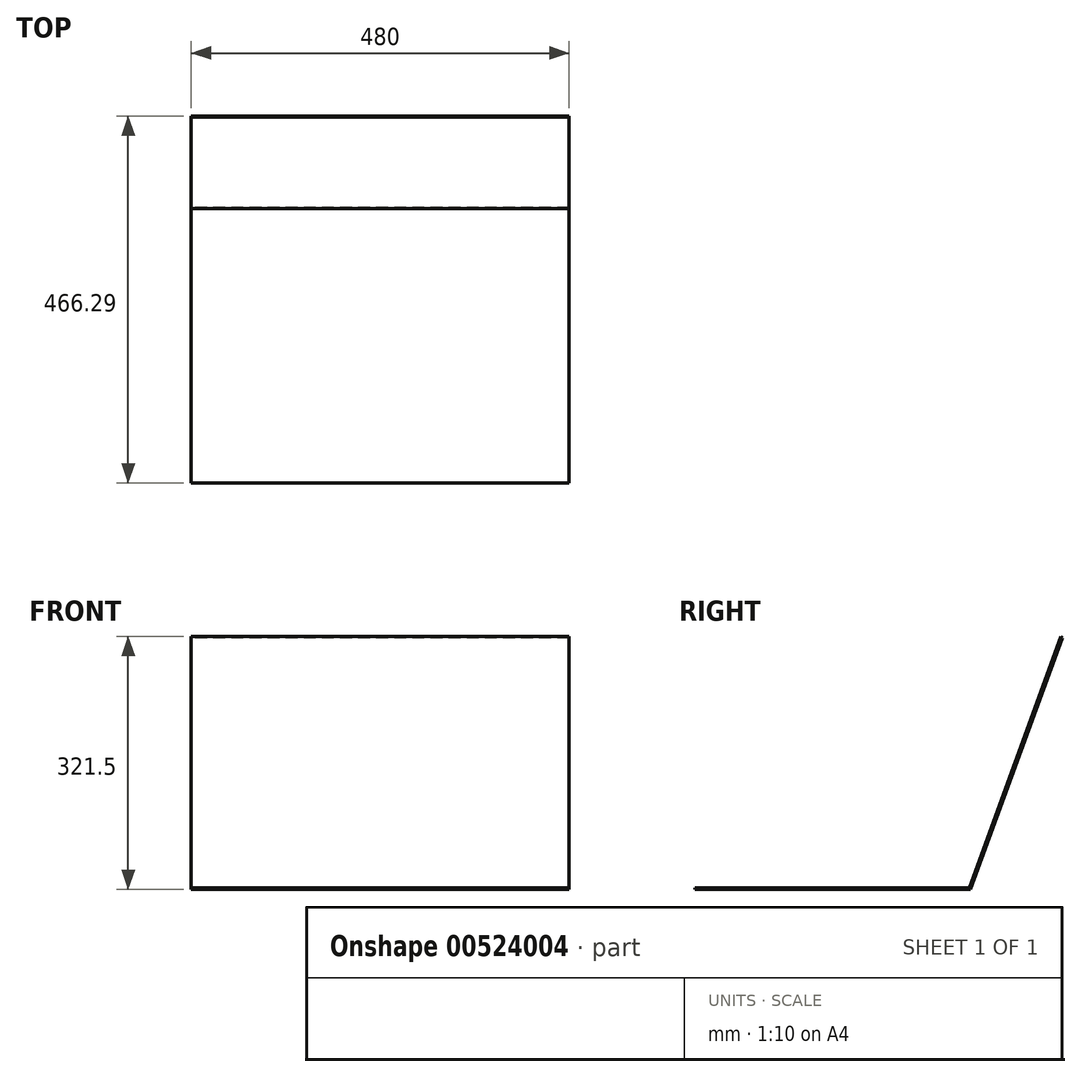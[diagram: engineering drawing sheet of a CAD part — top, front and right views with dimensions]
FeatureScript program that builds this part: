
annotation { "Feature Type Name" : "Feature", "Feature Type Description" : "" }
export const myFeature = defineFeature(function(context is Context, id is Id, definition is map)
    precondition{}
    {
        {
            var Q0;
            Q0=qCreatedBy(makeId("Right.planeOp"),FACE);
            var sketch = newSketch(context, id + "F0", { "sketchPlane" : qUnion([Q0])});
            skLineSegment(sketch, "E0", {"start": v(0, 0) * mm, "end": v(116.29, 319.5) * mm});
            skLineSegment(sketch, "E1", {"start": v(0, 0) * mm, "end": v(-350, 0) * mm});
            skLineSegment(sketch, "E2.0", {"start": v(-1.4, 2) * mm, "end": v(114.89, 321.5) * mm});
            skLineSegment(sketch, "E2.1", {"start": v(-1.4, 2) * mm, "end": v(-350, 2) * mm});
            skLineSegment(sketch, "E3", {"start": v(-350, 2) * mm, "end": v(-350, 0) * mm});
            skLineSegment(sketch, "E4", {"start": v(114.89, 321.5) * mm, "end": v(116.29, 319.5) * mm});
            skSolve(sketch);
        }
        {
            var Q0;
            Q0=makeQuery(id+"F0.imprint","IMPRINT",FACE,{"disambiguationData":[TD([[makeQuery(id+"F0.imprint","IMPRINT",EDGE,{"derivedFrom":sQuery(id+"F0.wireOp",EDGE,"E0")}),1.0]])]});
            extrude(context, id + "F1", {"entities" : qUnion([Q0]), "depth" : 480 * mm, "offsetDistance" : 25 * mm});
        }
    });
